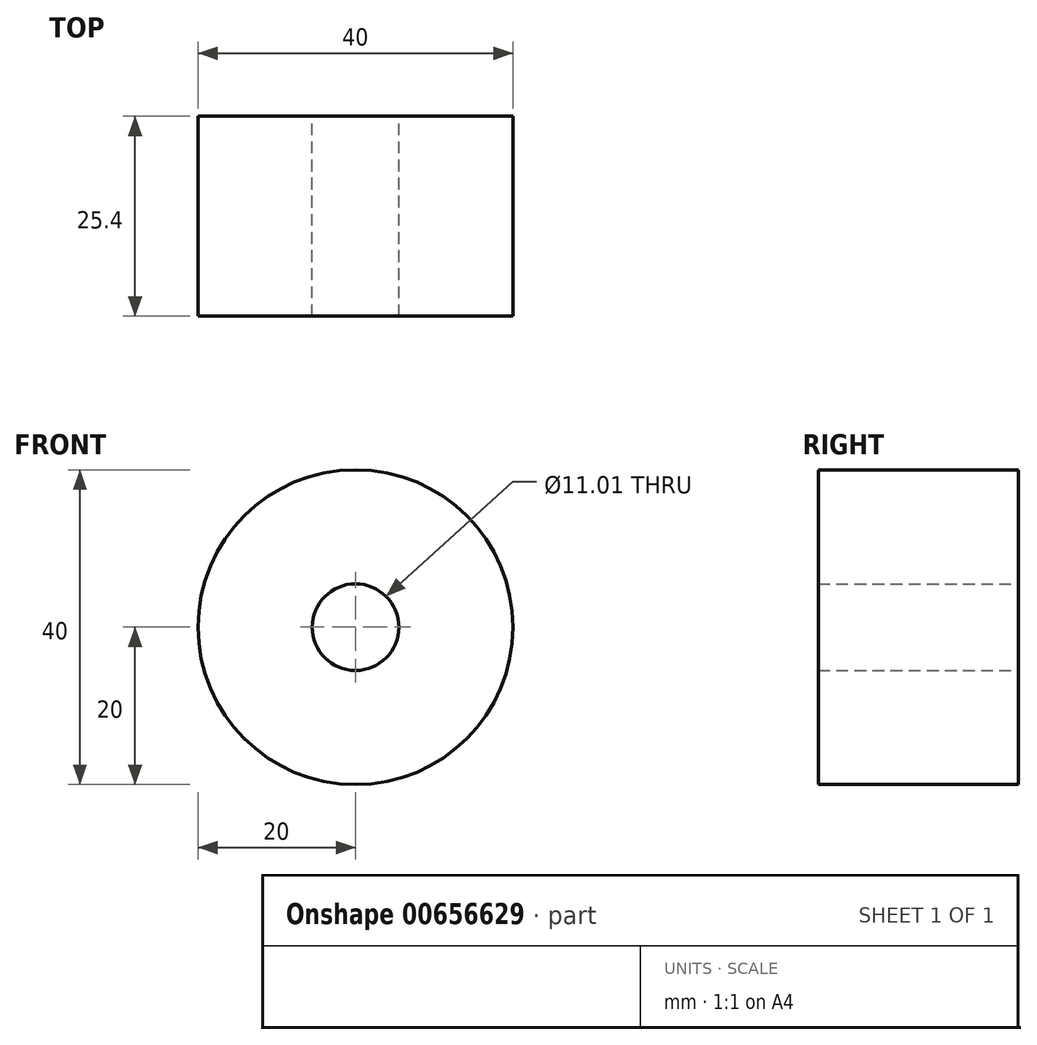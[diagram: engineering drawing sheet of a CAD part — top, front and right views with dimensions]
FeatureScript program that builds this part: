
annotation { "Feature Type Name" : "Feature", "Feature Type Description" : "" }
export const myFeature = defineFeature(function(context is Context, id is Id, definition is map)
    precondition{}
    {
        {
            var Q0;
            Q0=qCreatedBy(makeId("Front.planeOp"),FACE);
            var sketch = newSketch(context, id + "F0", { "sketchPlane" : qUnion([Q0])});
            skCircle(sketch, "E0", {"center": v(0, 0) * mm, "radius": 20 * mm});
            skCircle(sketch, "E1", {"center": v(0, 0) * mm, "radius": 5.5 * mm});
            skSolve(sketch);
        }
        {
            var Q0;
            Q0 = qSketchRegion(id + "F0", true);
            extrude(context, id + "F1", {"entities" : qUnion([Q0]), "depth" : 25.4 * mm, "offsetDistance" : 25.4 * mm});
        }
    });
